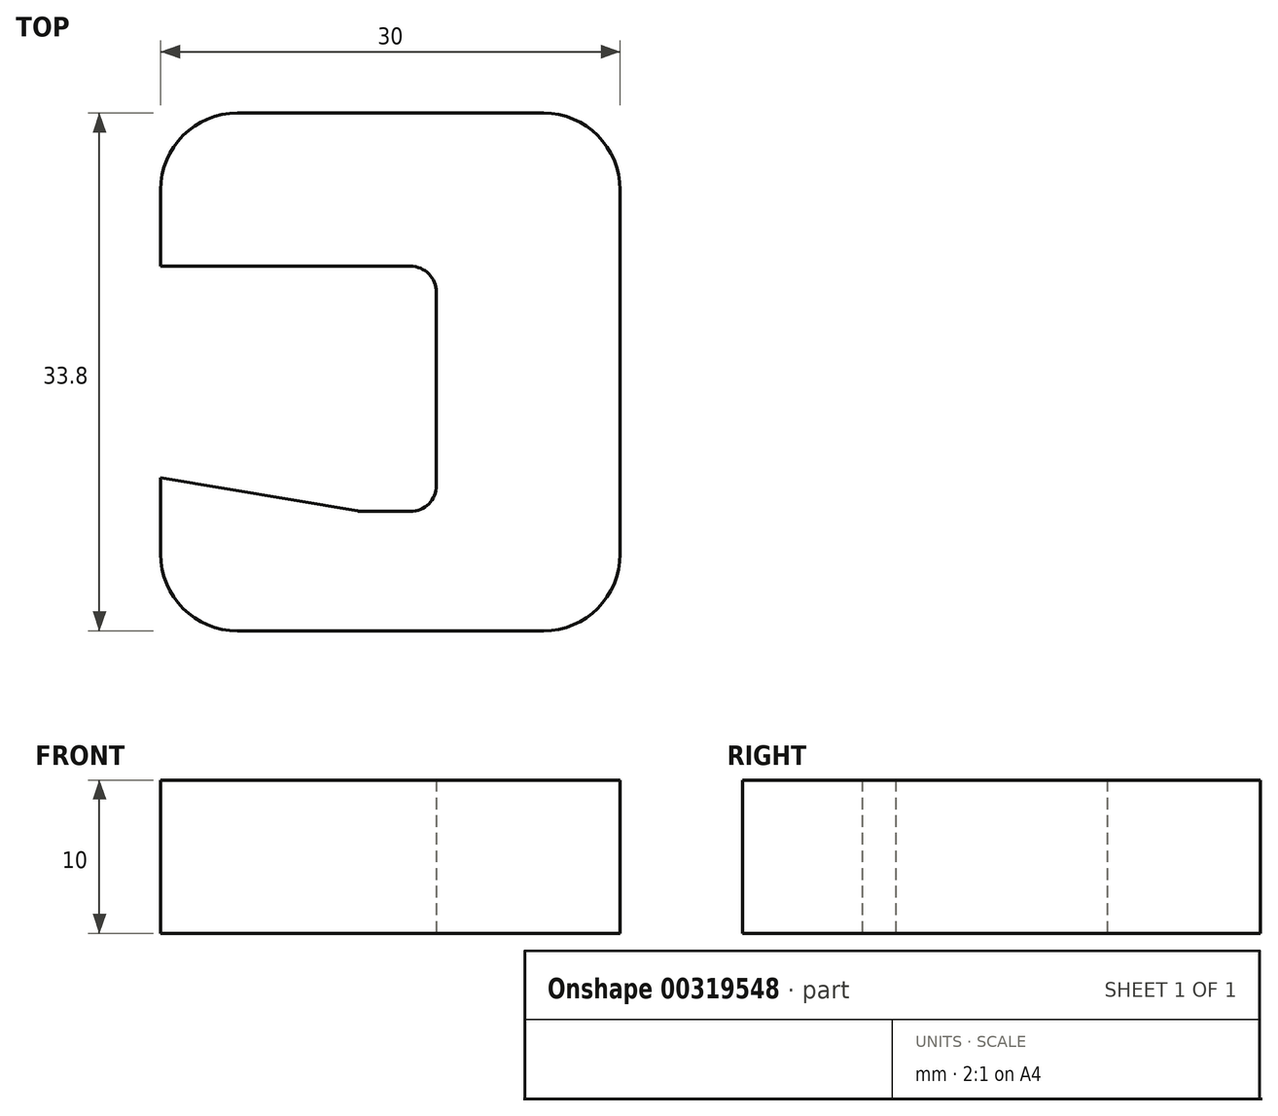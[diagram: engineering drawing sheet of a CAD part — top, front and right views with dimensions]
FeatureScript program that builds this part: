
annotation { "Feature Type Name" : "Feature", "Feature Type Description" : "" }
export const myFeature = defineFeature(function(context is Context, id is Id, definition is map)
    precondition{}
    {
        {
            var Q0;
            Q0=qCreatedBy(makeId("Top.planeOp"),FACE);
            var sketch = newSketch(context, id + "F0", { "sketchPlane" : qUnion([Q0])});
            skLineSegment(sketch, "E0", {"start": v(0, 0) * mm, "end": v(18, 0) * mm});
            skLineSegment(sketch, "E1", {"start": v(18, 0) * mm, "end": v(18, -16) * mm});
            skLineSegment(sketch, "E2", {"start": v(18, -16) * mm, "end": v(13, -16) * mm});
            skLineSegment(sketch, "E3", {"start": v(13, -16) * mm, "end": v(13, -13.8) * mm, "construction": true});
            skLineSegment(sketch, "E4", {"start": v(13, -13.8) * mm, "end": v(0, -13.8) * mm, "construction": true});
            skLineSegment(sketch, "E5", {"start": v(0, -13.8) * mm, "end": v(0, -23.8) * mm});
            skLineSegment(sketch, "E6", {"start": v(0, -23.8) * mm, "end": v(30, -23.8) * mm});
            skLineSegment(sketch, "E7", {"start": v(30, -23.8) * mm, "end": v(30, 10) * mm});
            skLineSegment(sketch, "E8", {"start": v(30, 10) * mm, "end": v(0, 10) * mm});
            skLineSegment(sketch, "E9", {"start": v(0, 10) * mm, "end": v(0, 0) * mm});
            skLineSegment(sketch, "E10", {"start": v(0, -13.8) * mm, "end": v(13, -16) * mm});
            skSolve(sketch);
        }
        {
            var Q0;
            Q0 = qSketchRegion(id + "F0", true);
            extrude(context, id + "F1", {"entities" : qUnion([Q0]), "depth" : 10 * mm});
        }
        {
            var Q0;
            Q0=makeQuery(id+"F1.opExtrude","SWEPT_EDGE",EDGE,{"disambiguationData":[OSD([sQuery(id+"F0.wireOp",EDGE,"E0"),sQuery(id+"F0.wireOp",EDGE,"E1")])]});
            var Q1;
            Q1=makeQuery(id+"F1.opExtrude","SWEPT_EDGE",EDGE,{"disambiguationData":[OSD([sQuery(id+"F0.wireOp",EDGE,"E1"),sQuery(id+"F0.wireOp",EDGE,"E2")])]});
            var Q2;
            Q2=makeQuery(id+"F1.opExtrude","SWEPT_EDGE",EDGE,{"disambiguationData":[OSD([sQuery(id+"F0.wireOp",EDGE,"E2"),sQuery(id+"F0.wireOp",EDGE,"E3")])]});
            fillet(context, id + "F2", {"entities" : qUnion([Q0, Q1, Q2]), "radius" : 1.69 * mm, "tangentPropagation" : true, "allowEdgeOverflow" : false});
        }
        {
            var Q0;
            Q0=makeQuery(id+"F1.opExtrude","SWEPT_EDGE",EDGE,{"disambiguationData":[OSD([sQuery(id+"F0.wireOp",EDGE,"E8"),sQuery(id+"F0.wireOp",EDGE,"E9")])]});
            var Q1;
            Q1=makeQuery(id+"F1.opExtrude","SWEPT_EDGE",EDGE,{"disambiguationData":[OSD([sQuery(id+"F0.wireOp",EDGE,"E7"),sQuery(id+"F0.wireOp",EDGE,"E8")])]});
            var Q2;
            Q2=makeQuery(id+"F1.opExtrude","SWEPT_EDGE",EDGE,{"disambiguationData":[OSD([sQuery(id+"F0.wireOp",EDGE,"E6"),sQuery(id+"F0.wireOp",EDGE,"E7")])]});
            var Q3;
            Q3=makeQuery(id+"F1.opExtrude","SWEPT_EDGE",EDGE,{"disambiguationData":[OSD([sQuery(id+"F0.wireOp",EDGE,"E5"),sQuery(id+"F0.wireOp",EDGE,"E6")])]});
            fillet(context, id + "F3", {"entities" : qUnion([Q0, Q1, Q2, Q3]), "radius" : 5 * mm, "tangentPropagation" : true, "allowEdgeOverflow" : false});
        }
    });
